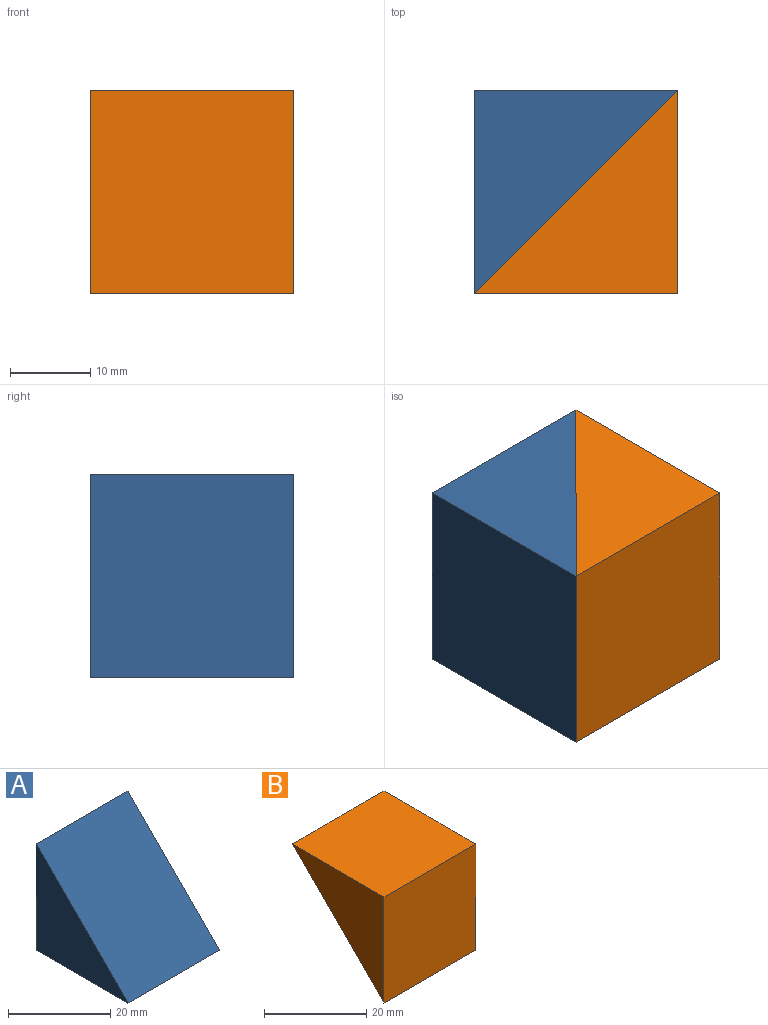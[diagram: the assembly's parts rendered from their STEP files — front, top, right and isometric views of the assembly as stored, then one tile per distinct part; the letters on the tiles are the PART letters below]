
ASSEMBLY  parts=2 mates=1
PART A: 5 faces, bbox 25.4x25.4x25.4 mm
  f0: plane 25.4x25.4mm, normal (0,0,-1), area 645.2mm2, adj f1,f2,f3,f4
  f1: plane 25.4x25.4mm, normal (0,-0.71,0.71), area 912.4mm2, adj f0,f2,f3,f4
  f2: plane 25.4x25.4mm, normal (0,1,0), area 645.2mm2, adj f0,f1,f3,f4
  f3: plane 25.4x25.4mm, normal (1,0,0), area 322.6mm2, adj f0,f1,f2
  f4: plane 25.4x25.4mm, normal (-1,0,0), area 322.6mm2, adj f0,f1,f2
PART B: 5 faces, bbox 25.4x25.4x25.4 mm
  f0: plane 25.4x25.4mm, normal (0,-1,0), area 645.2mm2, adj f1,f2,f3,f4
  f1: plane 25.4x25.4mm, normal (0,0.71,-0.71), area 912.4mm2, adj f0,f2,f3,f4
  f2: plane 25.4x25.4mm, normal (0,0,1), area 645.2mm2, adj f0,f1,f3,f4
  f3: plane 25.4x25.4mm, normal (1,0,0), area 322.6mm2, adj f0,f1,f2
  f4: plane 25.4x25.4mm, normal (-1,0,0), area 322.6mm2, adj f0,f1,f2
PLACE A rot(axis=(0,1,0),90deg) t=(0,-12.7,0)mm
PLACE B rot(axis=(0.58,-0.58,0.58),120deg) t=(0,-12.7,0)mm
MATE fastened A.f1 <-> B.f1  axis (0.71,-0.71,0) through (0,-12.7,0)mm
